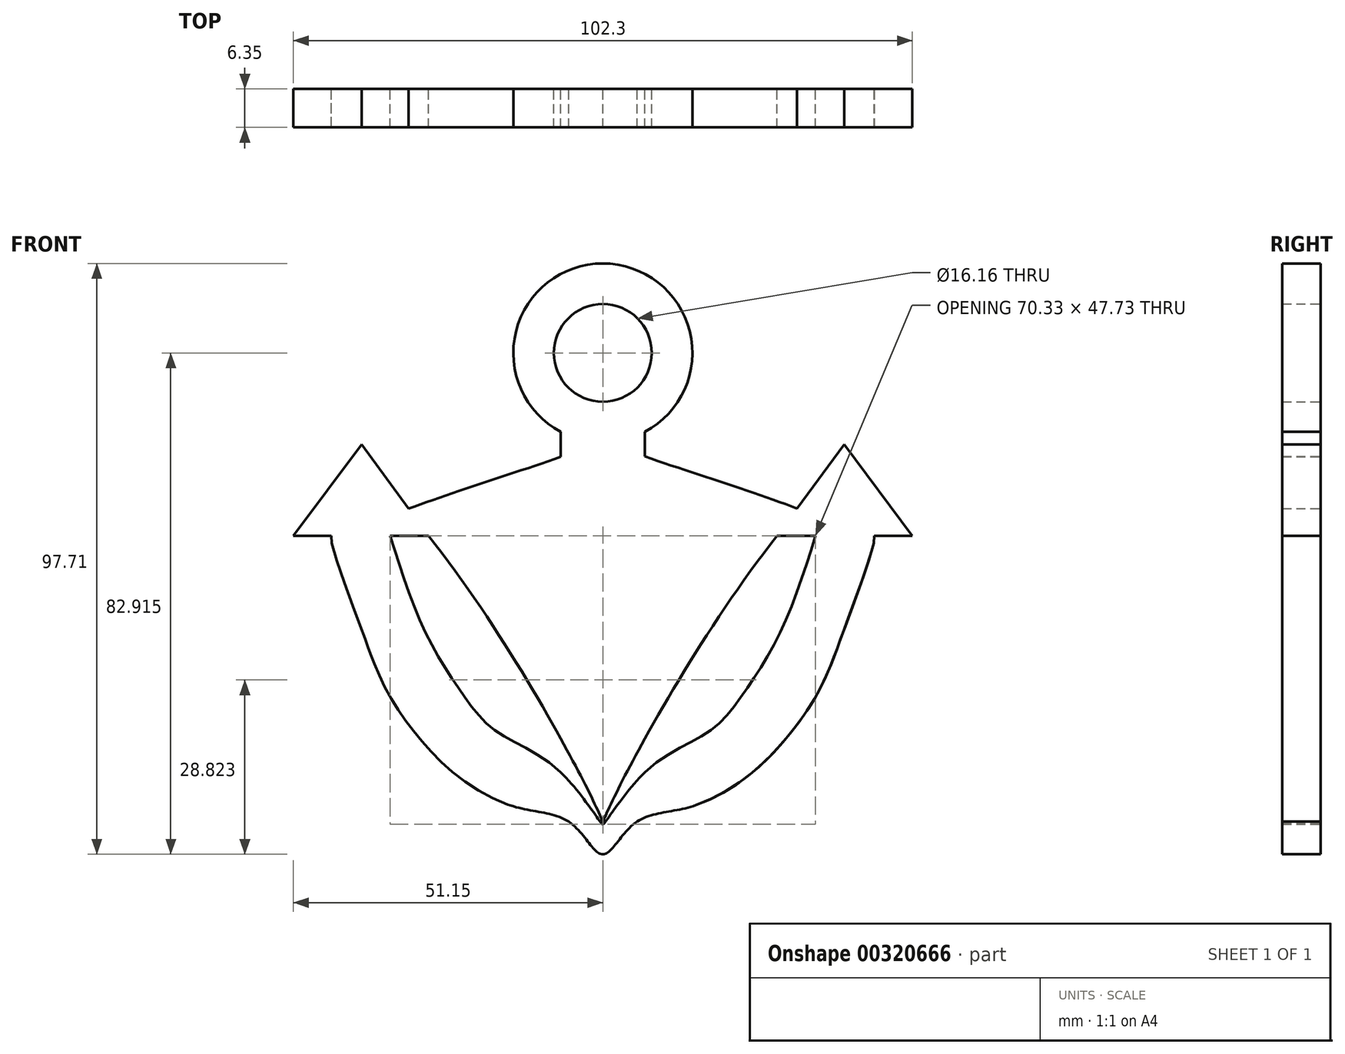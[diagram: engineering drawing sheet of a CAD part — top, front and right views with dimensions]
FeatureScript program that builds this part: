
annotation { "Feature Type Name" : "Feature", "Feature Type Description" : "" }
export const myFeature = defineFeature(function(context is Context, id is Id, definition is map)
    precondition{}
    {
        {
            var Q0;
            Q0=qCreatedBy(makeId("Front.planeOp"),FACE);
            var sketch = newSketch(context, id + "F0", { "sketchPlane" : qUnion([Q0])});
            skPoint(sketch, "E0.start.orphan", {"position": v(0, 30.2) * mm});
            skPoint(sketch, "E1", {"position": v(-17.06, -44.3) * mm});
            skPoint(sketch, "E2.1.internal.orphan", {"position": v(-52.97, -11.89) * mm});
            skPoint(sketch, "E2.13.internal.orphan", {"position": v(40.8, 0) * mm});
            skPoint(sketch, "E2.2.internal.orphan", {"position": v(-52.97, -21.37) * mm});
            skPoint(sketch, "E2.7.internal.orphan", {"position": v(0, -52.69) * mm});
            skPoint(sketch, "E3.1.internal.orphan", {"position": v(-8.98, -25.26) * mm});
            skPoint(sketch, "E3.3.internal.orphan", {"position": v(-34.21, -19.57) * mm});
            skPoint(sketch, "E4.orphan", {"position": v(-8.98, -19.57) * mm});
            skPoint(sketch, "E5.trimOffspring.6.internal.orphan", {"position": v(-5.09, -47.7) * mm});
            skPoint(sketch, "E5.trimOffspring.8.internal.orphan", {"position": v(5, -47.7) * mm});
            skPoint(sketch, "E6.start.orphan", {"position": v(-30.22, 0) * mm});
            skPoint(sketch, "E7.start.orphan", {"position": v(-52.97, 0) * mm});
            skPoint(sketch, "E8", {"position": v(44.8, 0) * mm});
            skLineSegment(sketch, "E9", {"start": v(44.8, 0) * mm, "end": v(51.15, 0) * mm});
            skLineSegment(sketch, "E10", {"start": v(51.15, 0) * mm, "end": v(39.87, 15.1) * mm});
            skLineSegment(sketch, "E11", {"start": v(39.87, 15.1) * mm, "end": v(28.82, 0) * mm});
            skLineSegment(sketch, "E12", {"start": v(28.82, 0) * mm, "end": v(35.17, 0) * mm});
            skFitSpline(sketch, "E13", {"points": [v(35.17, 0) * mm, v(29.71, -15.15) * mm, v(23.58, -25.62) * mm, v(17.6, -32.34) * mm, v(6.95, -39.14) * mm, v(0, -47.73) * mm, v(28.82, 0) * mm], "startDerivative": vector(-30.3, -94.71) * mm, "endDerivative": vector(157.84, 199.71) * mm});
            skLineSegment(sketch, "E14.MirrorCS", {"start": v(-39.87, 15.1) * mm, "end": v(-28.82, 0) * mm});
            skLineSegment(sketch, "E15.MirrorCS", {"start": v(-51.15, 0) * mm, "end": v(-39.87, 15.1) * mm});
            skLineSegment(sketch, "E16.MirrorCS", {"start": v(-44.8, 0) * mm, "end": v(-51.15, 0) * mm});
            skLineSegment(sketch, "E17.MirrorCS", {"start": v(-28.82, 0) * mm, "end": v(-35.17, 0) * mm});
            skFitSpline(sketch, "E18.MirrorCS", {"points": [v(-35.17, 0) * mm, v(-29.71, -15.15) * mm, v(-23.58, -25.62) * mm, v(-17.6, -32.34) * mm, v(-6.95, -39.14) * mm, v(0, -47.73) * mm, v(-28.82, 0) * mm], "startDerivative": vector(30.3, -94.71) * mm, "endDerivative": vector(-157.84, 199.71) * mm});
            skFitSpline(sketch, "E19.MirrorCS", {"points": [v(52.97, 0) * mm, v(52.97, -11.89) * mm, v(52.97, -21.37) * mm, v(42.1, -34.43) * mm, v(30.42, -40.72) * mm, v(17.06, -44.3) * mm, v(5.09, -47.7) * mm, v(0, -52.69) * mm, v(-5, -47.73) * mm, v(-14.27, -44.9) * mm, v(-24.74, -39.14) * mm, v(-31.25, -32.34) * mm, v(-35.73, -25.62) * mm, v(-38.42, -19.47) * mm, v(-40, -15.15) * mm, v(-44.8, 0) * mm, v(-40.38, -6.13) * mm, v(-40.89, -3.9) * mm, v(-40.8, 0) * mm, v(0, 15.74) * mm, v(8.98, 29.8) * mm], "startDerivative": vector(-9.2, -202.57) * mm, "endDerivative": vector(-14.7, 392.88) * mm});
            skPoint(sketch, "E20.orphan", {"position": v(0, 51.53) * mm});
            skArc(sketch, "E21", {"start": v(6.95, 17.16) * mm, "mid": v(0, 45.02) * mm, "end": v(-6.95, 17.16) * mm});
            skLineSegment(sketch, "E22", {"start": v(-6.95, -39.14) * mm, "end": v(-6.95, 17.16) * mm});
            skLineSegment(sketch, "E23", {"start": v(6.95, -39.14) * mm, "end": v(6.95, 17.16) * mm});
            skPoint(sketch, "E24.start.orphan", {"position": v(3.04, 15.74) * mm});
            skFitSpline(sketch, "E25.trimOffspring", {"points": [v(-52.97, 0) * mm, v(-52.97, -11.89) * mm, v(-52.97, -21.37) * mm, v(-30.42, -40.72) * mm, v(-17.06, -44.3) * mm, v(-5.09, -47.7) * mm, v(0, -52.69) * mm, v(5, -47.73) * mm, v(14.27, -44.9) * mm, v(24.74, -39.14) * mm, v(31.25, -32.34) * mm, v(35.73, -25.62) * mm, v(38.42, -19.47) * mm, v(40, -15.15) * mm, v(44.8, 0) * mm, v(40.38, -6.13) * mm, v(40.89, -3.9) * mm, v(40.8, 0) * mm, v(0, 15.74) * mm, v(-8.98, 29.8) * mm], "startDerivative": vector(9.2, -202.57) * mm, "endDerivative": vector(14.7, 392.88) * mm});
            skCircle(sketch, "E26", {"center": v(0, 30.22) * mm, "radius": 8.08 * mm});
            skSolve(sketch);
        }
        {
            var Q0;
            Q0 = qSketchRegion(id + "F0", true);
            extrude(context, id + "F1", {"entities" : qUnion([Q0]), "depth" : 6.35 * mm});
        }
    });
